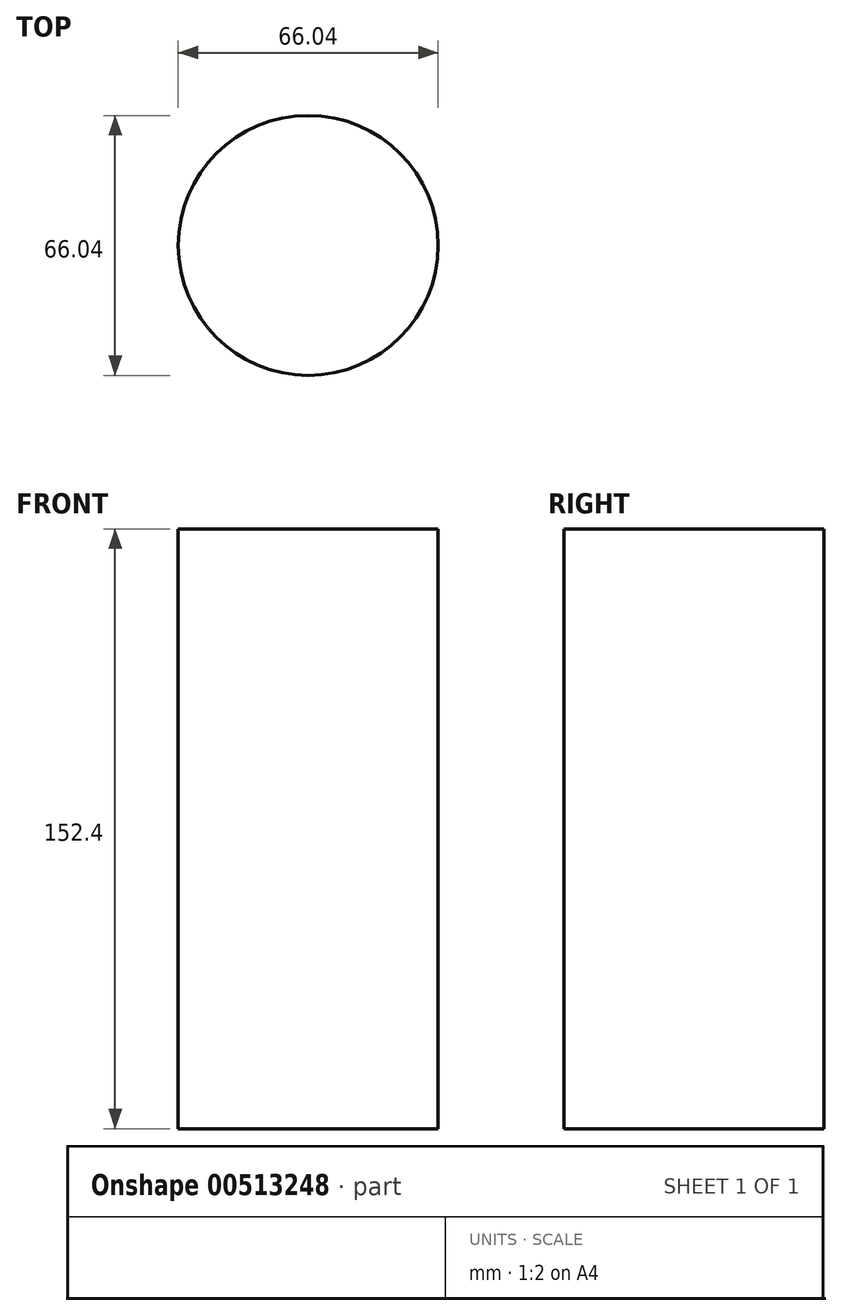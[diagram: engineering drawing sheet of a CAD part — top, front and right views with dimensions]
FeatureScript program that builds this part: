
annotation { "Feature Type Name" : "Feature", "Feature Type Description" : "" }
export const myFeature = defineFeature(function(context is Context, id is Id, definition is map)
    precondition{}
    {
        {
            var Q0;
            Q0=qCreatedBy(makeId("Top.planeOp"),FACE);
            var sketch = newSketch(context, id + "F0", { "sketchPlane" : qUnion([Q0])});
            skCircle(sketch, "E0", {"center": v(0, 0) * mm, "radius": 33.02 * mm});
            skSolve(sketch);
        }
        {
            var Q0;
            Q0=makeQuery(id+"F0.imprint","IMPRINT",FACE,{"disambiguationData":[TD([[makeQuery(id+"F0.imprint","IMPRINT",EDGE,{"derivedFrom":sQuery(id+"F0.wireOp",EDGE,"E0")}),1.0]])]});
            extrude(context, id + "F1", {"entities" : qUnion([Q0]), "depth" : 152.4 * mm});
        }
    });
